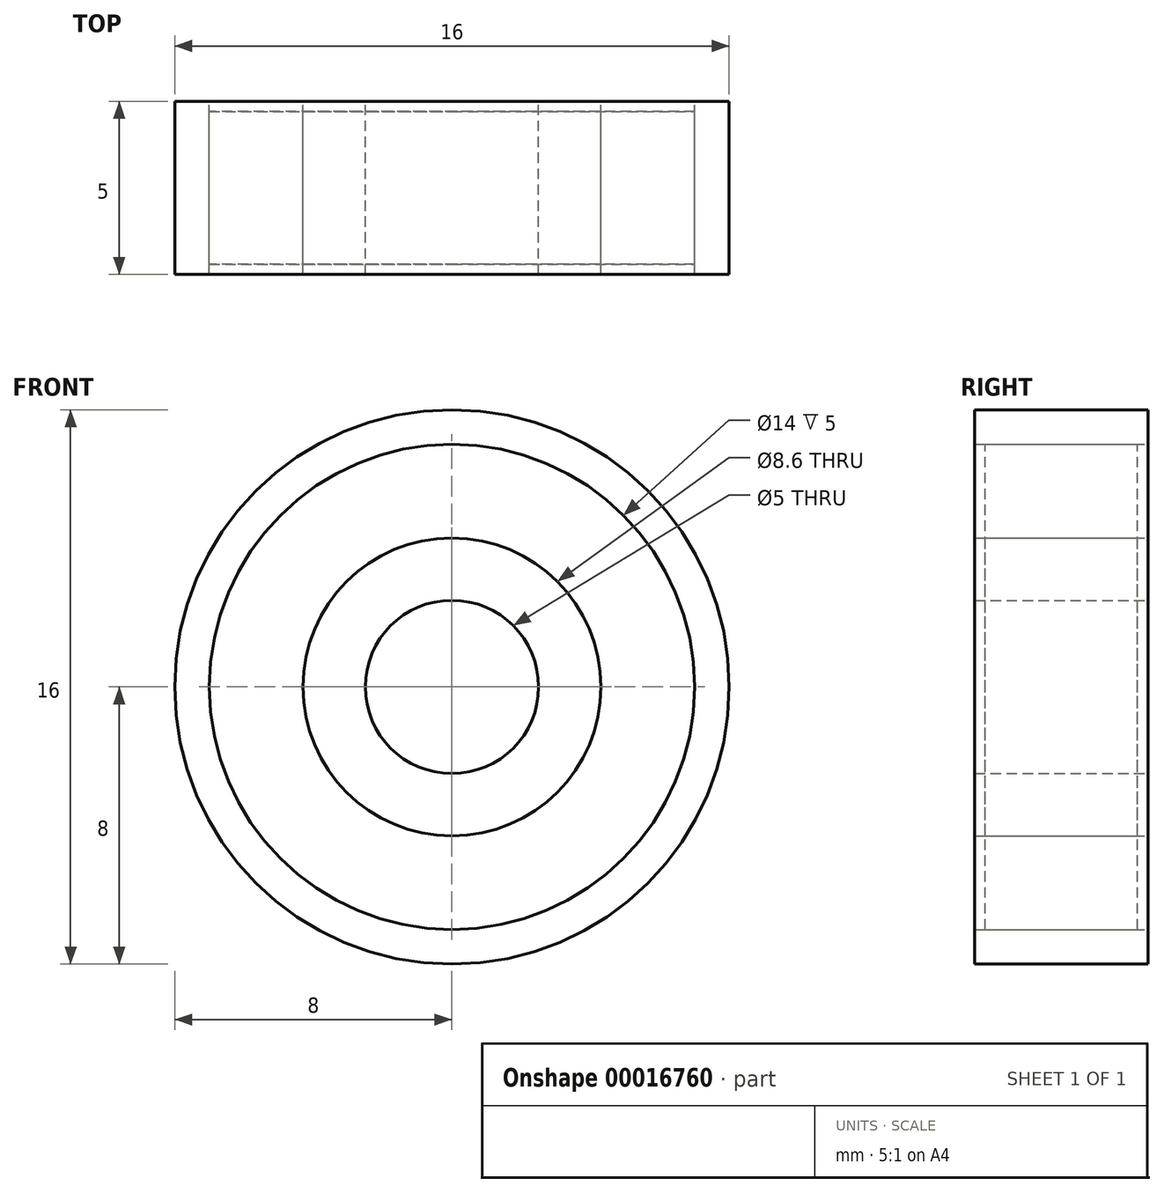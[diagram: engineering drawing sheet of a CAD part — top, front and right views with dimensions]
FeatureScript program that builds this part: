
annotation { "Feature Type Name" : "Feature", "Feature Type Description" : "" }
export const myFeature = defineFeature(function(context is Context, id is Id, definition is map)
    precondition{}
    {
        {
            var Q0;
            Q0=qCreatedBy(makeId("Front.planeOp"),FACE);
            var sketch = newSketch(context, id + "F0", { "sketchPlane" : qUnion([Q0])});
            skCircle(sketch, "E0", {"center": v(0, 0) * mm, "radius": 2.5 * mm});
            skCircle(sketch, "E1", {"center": v(0, 0) * mm, "radius": 4.3 * mm});
            skCircle(sketch, "E2", {"center": v(0, 0) * mm, "radius": 7 * mm});
            skCircle(sketch, "E3", {"center": v(0, 0) * mm, "radius": 8 * mm});
            skSolve(sketch);
        }
        {
            var Q0;
            Q0=makeQuery(id+"F0.imprint","IMPRINT",FACE,{"disambiguationData":[TD([[makeQuery(id+"F0.imprint","IMPRINT",EDGE,{"derivedFrom":sQuery(id+"F0.wireOp",EDGE,"E0")}),-1.0]])]});
            extrude(context, id + "F1", {"entities" : qUnion([Q0]), "endBound" : BoundingType.SYMMETRIC, "depth" : 5 * mm});
        }
        {
            var Q0;
            Q0=makeQuery(id+"F0.imprint","IMPRINT",FACE,{"disambiguationData":[TD([[makeQuery(id+"F0.imprint","IMPRINT",EDGE,{"derivedFrom":sQuery(id+"F0.wireOp",EDGE,"E2")}),-1.0]])]});
            extrude(context, id + "F2", {"entities" : qUnion([Q0]), "endBound" : BoundingType.SYMMETRIC, "depth" : 5 * mm});
        }
        {
            var Q0;
            Q0=makeQuery(id+"F0.imprint","IMPRINT",FACE,{"disambiguationData":[TD([[makeQuery(id+"F0.imprint","IMPRINT",EDGE,{"derivedFrom":sQuery(id+"F0.wireOp",EDGE,"E1")}),-1.0]])]});
            extrude(context, id + "F3", {"entities" : qUnion([Q0]), "endBound" : BoundingType.SYMMETRIC, "depth" : 4.4 * mm});
        }
    });
